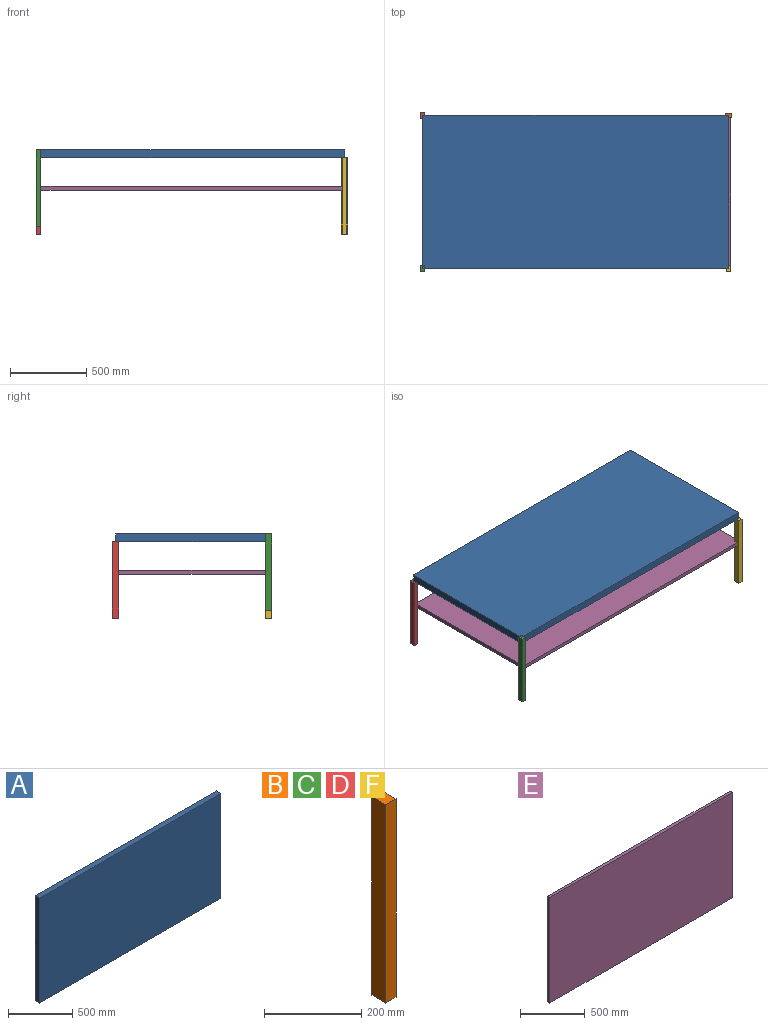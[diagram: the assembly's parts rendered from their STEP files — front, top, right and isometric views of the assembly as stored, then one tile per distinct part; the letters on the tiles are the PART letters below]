
ASSEMBLY  parts=6 mates=5
PART A: 6 faces, bbox 2000x50x1000 mm
  f0: plane 2000x50mm, normal (0,0,1), area 100000mm2, adj f1,f3,f4,f5
  f1: plane 1000x50mm, normal (-1,0,0), area 50000mm2, adj f0,f2,f4,f5
  f2: plane 2000x50mm, normal (0,0,-1), area 100000mm2, adj f1,f3,f4,f5
  f3: plane 1000x50mm, normal (1,0,0), area 50000mm2, adj f0,f2,f4,f5
  f4: plane 2000x1000mm, normal (0,-1,0), area 2000000mm2, adj f0,f1,f2,f3
  f5: plane 2000x1000mm, normal (0,1,0), area 2000000mm2, adj f0,f1,f2,f3
PART B: 6 faces, bbox 30x40x500 mm
  f0: plane 40x30mm, normal (0,0,1), area 1200mm2, adj f1,f3,f4,f5
  f1: plane 500x40mm, normal (-1,0,0), area 20000mm2, adj f0,f2,f4,f5
  f2: plane 40x30mm, normal (0,0,-1), area 1200mm2, adj f1,f3,f4,f5
  f3: plane 500x40mm, normal (1,0,0), area 20000mm2, adj f0,f2,f4,f5
  f4: plane 500x30mm, normal (0,-1,0), area 15000mm2, adj f0,f1,f2,f3
  f5: plane 500x30mm, normal (0,1,0), area 15000mm2, adj f0,f1,f2,f3
PART C: same geometry as B
PART D: same geometry as B
PART E: 6 faces, bbox 2000x25x1000 mm
  f0: plane 2000x25mm, normal (0,0,1), area 50000mm2, adj f1,f3,f4,f5
  f1: plane 1000x25mm, normal (-1,0,0), area 25000mm2, adj f0,f2,f4,f5
  f2: plane 2000x25mm, normal (0,0,-1), area 50000mm2, adj f1,f3,f4,f5
  f3: plane 1000x25mm, normal (1,0,0), area 25000mm2, adj f0,f2,f4,f5
  f4: plane 2000x1000mm, normal (0,-1,0), area 2000000mm2, adj f0,f1,f2,f3
  f5: plane 2000x1000mm, normal (0,1,0), area 2000000mm2, adj f0,f1,f2,f3
PART F: same geometry as B
PLACE A rot(axis=(1,0,0),90deg) t=(-7.5,1063.32,351.48)mm
PLACE B rot(axis=(0.71,0.71,0),180deg) t=(2012.5,1048.32,301.48)mm
PLACE C t=(-22.5,83.32,-148.52)mm fixed
PLACE D t=(-22.5,1083.32,-198.52)mm
PLACE E rot(axis=(0,0.71,0.71),180deg) t=(2007.5,63.32,113.98)mm
PLACE F rot(axis=(1,0,0),180deg) t=(1977.5,43.32,301.48)mm
MATE fastened B.f2 <-> A.f4  axis (0,0,1) through (1992.5,1063.32,301.48)mm
MATE fastened F.f2 <-> A.f4  axis (0,0,1) through (1992.5,63.32,301.48)mm
MATE fastened C.f3 <-> E.f3  axis (1,0,0) through (7.5,63.32,101.48)mm
MATE fastened D.f0 <-> A.f4  axis (0,0,1) through (-7.5,1063.32,301.48)mm
MATE fastened C.f0 <-> A.f5  axis (0,0,1) through (-7.5,63.32,351.48)mm
